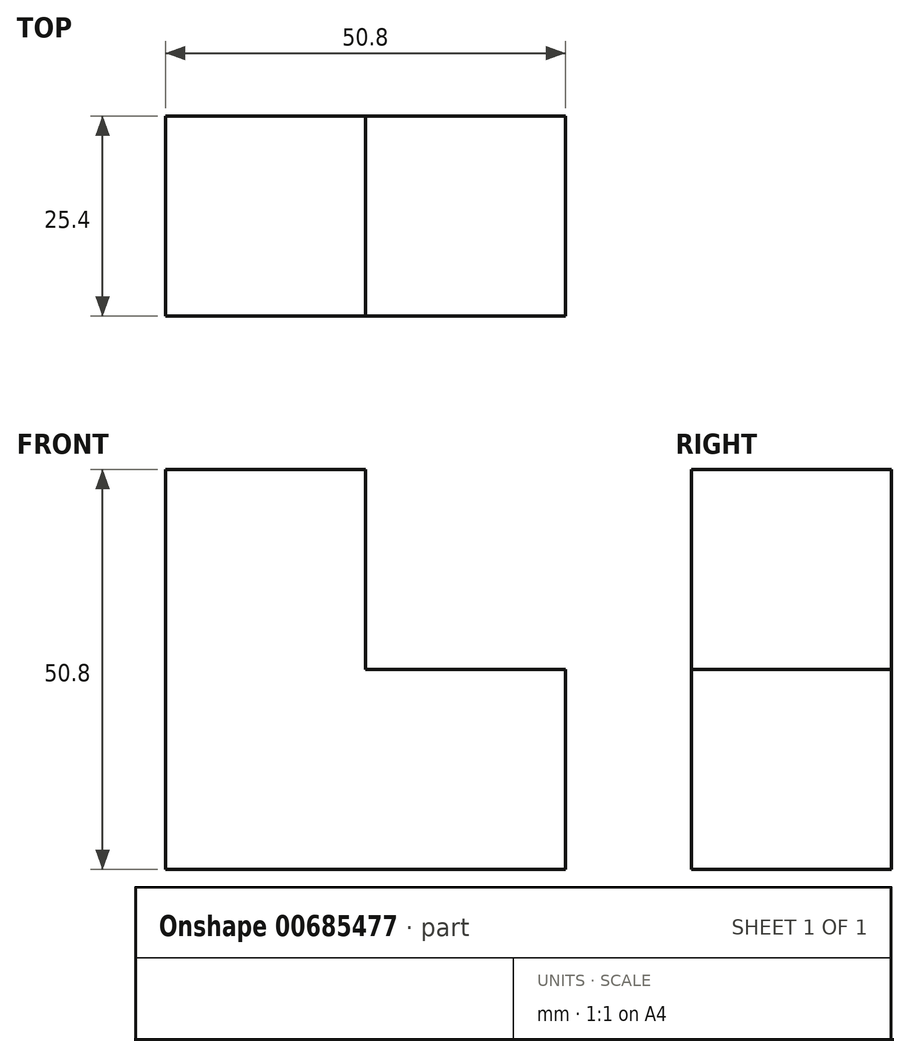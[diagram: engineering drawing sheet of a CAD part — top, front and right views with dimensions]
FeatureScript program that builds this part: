
annotation { "Feature Type Name" : "Feature", "Feature Type Description" : "" }
export const myFeature = defineFeature(function(context is Context, id is Id, definition is map)
    precondition{}
    {
        {
            var Q0;
            Q0=qCreatedBy(makeId("Front.planeOp"),FACE);
            var sketch = newSketch(context, id + "F0", { "sketchPlane" : qUnion([Q0])});
            skLineSegment(sketch, "E0", {"start": v(-50.8, 57.47) * mm, "end": v(-50.8, 6.67) * mm});
            skLineSegment(sketch, "E1", {"start": v(-50.8, 6.67) * mm, "end": v(0, 6.67) * mm});
            skLineSegment(sketch, "E2", {"start": v(-50.8, 57.47) * mm, "end": v(-25.4, 57.47) * mm});
            skLineSegment(sketch, "E3", {"start": v(-25.4, 57.47) * mm, "end": v(-25.4, 32.07) * mm});
            skLineSegment(sketch, "E4", {"start": v(-25.4, 32.07) * mm, "end": v(0, 32.07) * mm});
            skLineSegment(sketch, "E5", {"start": v(0, 32.07) * mm, "end": v(0, 6.67) * mm});
            skSolve(sketch);
        }
        {
            var Q0;
            Q0 = qSketchRegion(id + "F0", true);
            extrude(context, id + "F1", {"entities" : qUnion([Q0]), "depth" : 25.4 * mm, "offsetDistance" : 25.4 * mm});
        }
    });
